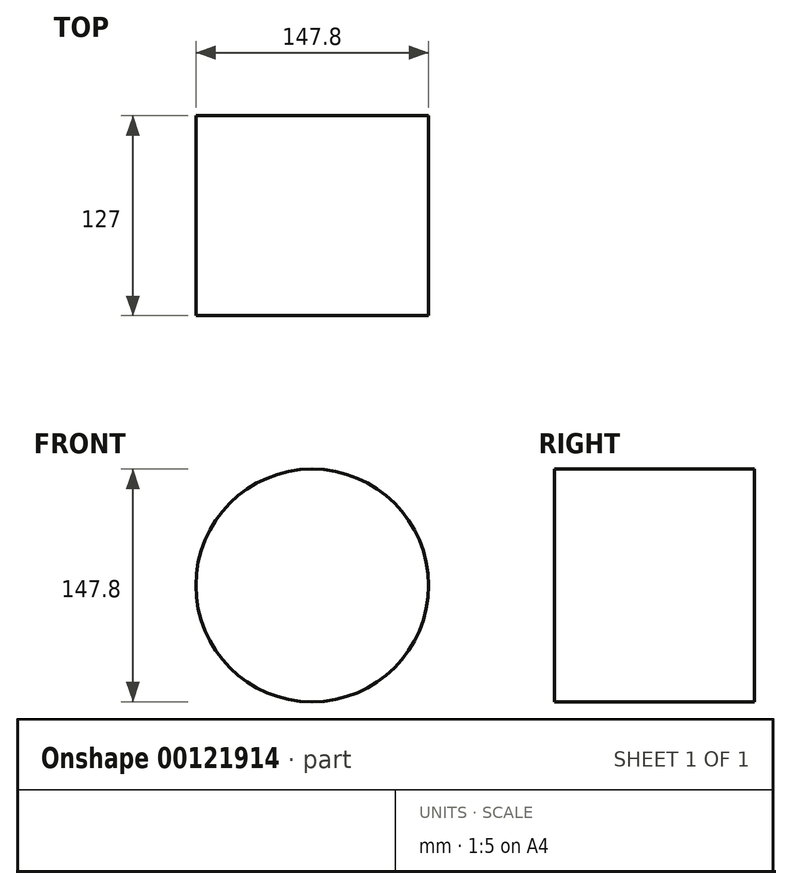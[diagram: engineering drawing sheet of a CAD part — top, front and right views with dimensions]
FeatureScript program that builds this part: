
annotation { "Feature Type Name" : "Feature", "Feature Type Description" : "" }
export const myFeature = defineFeature(function(context is Context, id is Id, definition is map)
    precondition{}
    {
        {
            var Q0;
            Q0=qCreatedBy(makeId("Front.planeOp"),FACE);
            var sketch = newSketch(context, id + "F0", { "sketchPlane" : qUnion([Q0])});
            skCircle(sketch, "E0", {"center": v(0, 0) * mm, "radius": 84.63 * mm});
            skCircle(sketch, "E1", {"center": v(0, 0) * mm, "radius": 78.27 * mm});
            skSolve(sketch);
        }
        {
            var Q0;
            Q0=sQuery(id+"F0.wireOp",EDGE,"E0");
            extrude(context, id + "F1", {"bodyType" : ToolBodyType.SURFACE, "surfaceEntities" : qUnion([Q0]), "depth" : 152.4 * mm});
        }
        {
            var Q0;
            Q0=qCreatedBy(makeId("Front.planeOp"),FACE);
            var sketch = newSketch(context, id + "F2", { "sketchPlane" : qUnion([Q0])});
            skCircle(sketch, "E2", {"center": v(0, 0) * mm, "radius": 73.9 * mm});
            skSolve(sketch);
        }
        {
            var Q0;
            Q0 = qSketchRegion(id + "F2", true);
            extrude(context, id + "F3", {"entities" : qUnion([Q0]), "depth" : 127 * mm});
        }
    });
